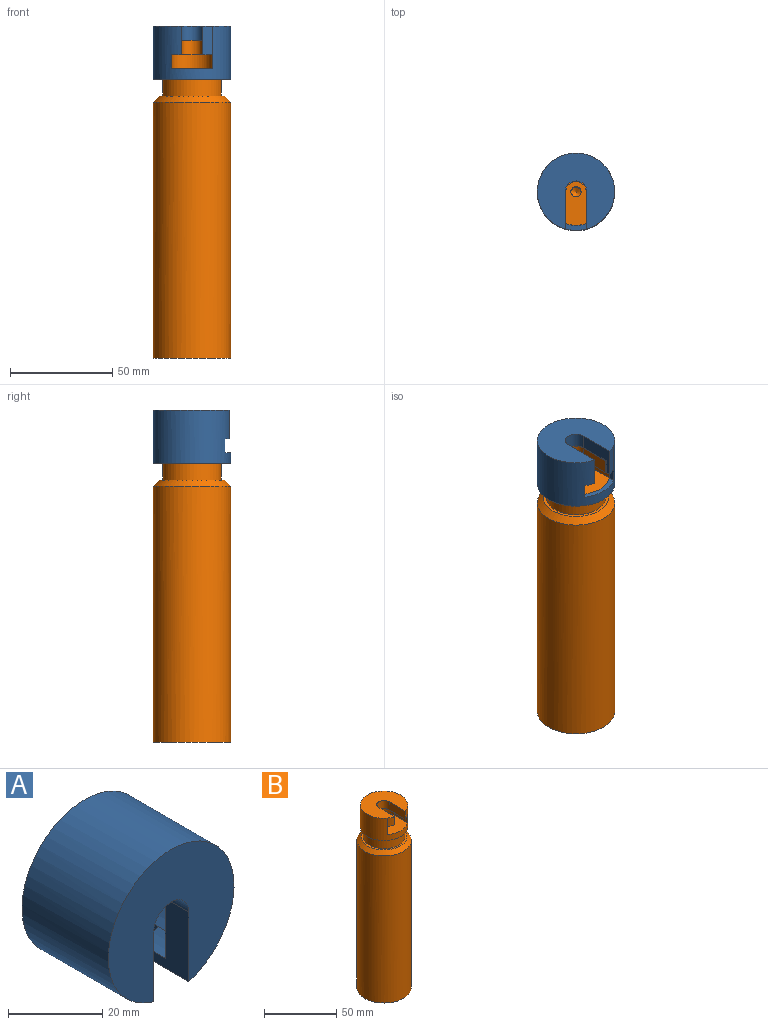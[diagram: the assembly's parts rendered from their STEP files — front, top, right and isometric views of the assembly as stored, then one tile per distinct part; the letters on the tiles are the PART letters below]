
ASSEMBLY  parts=2 mates=1
PART A: 15 faces, bbox 37.8x26x37.8 mm
  f0: plane 37.8x37.06mm, normal (0,-1,0), area 883mm2, adj f3,f4,f12,f13,f14
  f1: cylinder r=16.45mm len=32.9mm, axis (0,1,0), area 1700.7mm2, adj f2,f5,f6,f7,f8,f9,f11,f12
  f2: cylinder r=16.45mm len=7mm, axis (0,1,0), area 37.8mm2, adj f1,f6,f10,f13
  f3: cylinder r=18.9mm len=37.8mm, axis (0,1,0), area 2718mm2, adj f0,f4,f5,f7,f8,f9,f11,f12
  f4: cylinder r=18.9mm len=14mm, axis (0,1,0), area 73mm2, adj f0,f3,f10,f13
  f5: plane 37.8x37.8mm, normal (0,1,0), area 272.1mm2, adj f1,f3
  f6: plane 32.9x32.04mm, normal (0,1,0), area 637.1mm2, adj f1,f2,f12,f13,f14
  f7: plane 20x5.84mm, normal (0,-1,0), area 52.1mm2, adj f1,f3,f8,f11
  f8: plane 7x2.98mm, normal (1,0,0), area 20.8mm2, adj f1,f3,f7,f9
  f9: plane 5.09x4.75mm, normal (0,1,0), area 13mm2, adj f1,f3,f8,f12
  f10: plane 5.09x4.75mm, normal (0,1,0), area 13mm2, adj f2,f4,f11,f13
  f11: plane 7x2.98mm, normal (-1,0,0), area 20.8mm2, adj f1,f3,f7,f10
  f12: plane 18.16x14mm, normal (1,0,0), area 145.1mm2, adj f0,f1,f3,f6,f9,f14
  f13: plane 18.16x14mm, normal (-1,0,0), area 145.1mm2, adj f0,f2,f4,f6,f10,f14
  f14: cylinder r=5.25mm len=10.5mm, axis (0,-1,0), area 115.5mm2, adj f0,f6,f12,f13
PART B: 19 faces, bbox 37.8x37.8x155.3 mm
  f0: plane 25.62x20mm, normal (0,0,-1), area 262.7mm2, adj f6,f7,f9,f10,f11,f13,f14,f15
  f1: plane 26.4x20mm, normal (0,0,1), area 443.8mm2, adj f7,f9,f10,f11,f17
  f2: cylinder r=14.42mm len=28.84mm, axis (0,0,1), area 752mm2, adj f3,f8
  f3: plane 31.8x31.8mm, normal (0,0,1), area 141mm2, adj f2,f18
  f4: cylinder r=18.9mm len=125mm, axis (0,0,1), area 14844mm2, adj f5,f18
  f5: plane 37.8x37.8mm, normal (0,0,-1), area 1122.2mm2, adj f4
  f6: cylinder r=16.4mm len=7mm, axis (0,0,-1), area 39.7mm2, adj f0,f7,f12,f14
  f7: cylinder r=16.4mm len=32.8mm, axis (0,0,-1), area 1696.4mm2, adj f0,f1,f6,f8,f9,f11,f12,f15
  f8: plane 32.8x32.8mm, normal (0,0,-1), area 191.7mm2, adj f2,f7
  f9: plane 13x7mm, normal (1,0,0), area 91mm2, adj f0,f1,f7,f10
  f10: cylinder r=10mm len=20mm, axis (0,0,-1), area 219.9mm2, adj f0,f1,f9,f11
  f11: plane 13x7mm, normal (-1,0,0), area 91mm2, adj f0,f1,f7,f10
  f12: plane 32.8x32.02mm, normal (0,0,1), area 644.3mm2, adj f6,f7,f13,f14,f15
  f13: cylinder r=5mm len=10mm, axis (0,0,1), area 110mm2, adj f0,f12,f14,f15
  f14: plane 15.62x7mm, normal (1,0,0), area 109.3mm2, adj f0,f6,f12,f13
  f15: plane 15.62x7mm, normal (-1,0,0), area 109.3mm2, adj f0,f7,f12,f13
  f16: cone r=0mm half-angle=59deg, axis (0,0,1), area 22.9mm2, adj f17
  f17: cylinder r=2.5mm len=135mm, axis (0,0,1), area 2120.6mm2, adj f1,f16
  f18: cone r=15.9mm half-angle=45deg, axis (0,0,-1), area 463.8mm2, adj f3,f4
PLACE A rot(axis=(-1,0,0),90deg) t=(-41.97,-13.17,75.25)mm
PLACE B t=(-41.97,-13.17,-12.1)mm
MATE revolute A.f1 <-> B.f6  axis (0,0,-1) through (-41.97,-13.17,94.25)mm
